# Revit family: Beam-Clamp-Atkore-P2787
name_source: partatom
category: Specialty Equipment
revit_build: Autodesk Revit MEP 2012 (Build: 20110309_2315)
units: mm (PartAtom-declared; Revit-internal decimal feet)

## types (1)
- P2787
    04 CSI = 26 05 48
    95 CSI = 16070
    Assembly Code = D5090300
    Description = Beam Clamp
    Load Capacity Note = Visit the product page for load application and capacity.
    Manufacturer = Unistrut by Atkore International
    Manufacturer Fax = 708-339-7814
    Material = Multiple Options - See Catalog
    Model = P2787
    Overall Depth = 59.12 mm
    Overall Height = 90.18 mm
    Overall Width = 76.2 mm  [stored 0.25 ft]
    Part Number = P2787
    Part Type = Clamp
    Subcategory = Beam Clamp
    Thickness Gauge = 38.1 mm  [stored 0.125 ft]
    URL = http://unistrut.us
    Unit = Metal - Aluminum - Atkore - Electro - Galvanized

note: [stored X ft] marks values corroborated as IEEE doubles in the binary element streams (Revit-internal decimal feet)

## geometry (parser evidence)
native form markers: Blend x4, Sweep x3
no freeform markers — native parametric forms only
